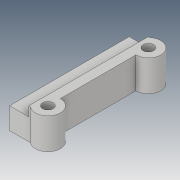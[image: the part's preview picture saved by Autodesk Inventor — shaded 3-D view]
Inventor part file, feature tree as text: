
AUTODESK INVENTOR PART (.ipt)
format: ipt  version: 2019 (Build 230136000, 136)  size: 117,760 bytes
history: native  units: mm
features: extrude x3, sketch x2
ambient origin geometry x8: Origin, YZ Plane, XZ Plane, XY Plane, X Axis, Y Axis, Z Axis, Center Point
bodies: Solid1 (feature_tree)
feature tree (5):
  extrude  "Extrusion1"  Depth=6.0mm
  sketch  "Sketch2"  dims[d2=4.5mm d3=0.0mm d4=2.0mm d5=2.2mm d6=0.0mm d8=2.0mm d9=2.2mm d10=0.0mm d11=2.0mm d17=1.5mm d18=1.5mm d19=2.0mm d20=4.5mm d21=0.0mm d22=0.0mm d23=2.0mm d24=0.0mm]
  extrude  "Extrusion3"  Depth=2.0mm
  extrude  "Extrusion4"  Depth=2.0mm
  sketch  "Sketch1"  dims[d0=25.0mm d1=6.0mm]
